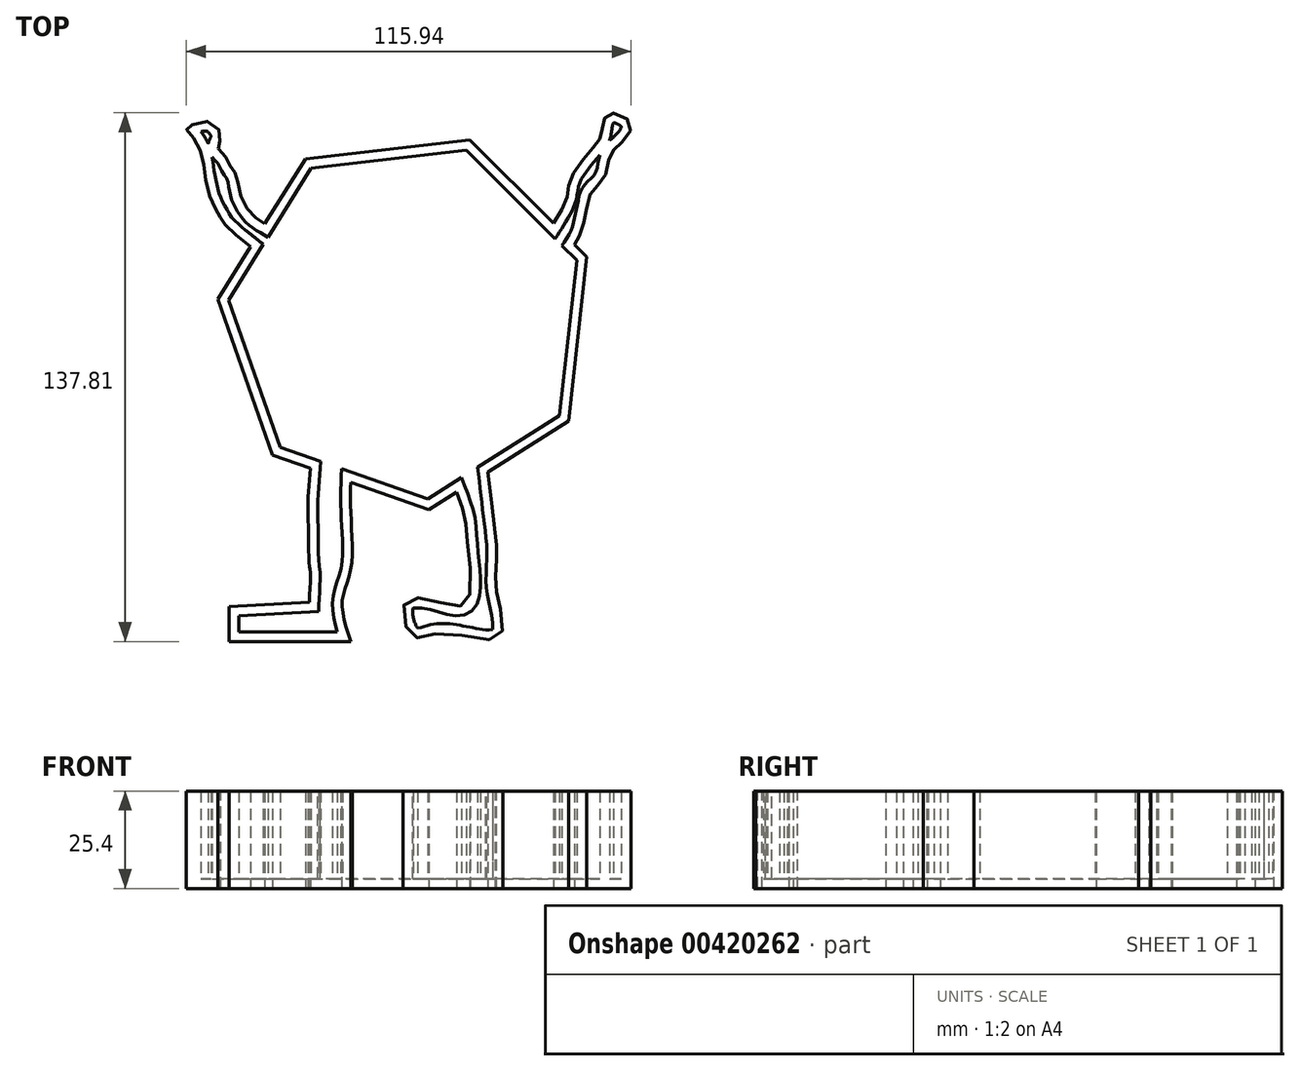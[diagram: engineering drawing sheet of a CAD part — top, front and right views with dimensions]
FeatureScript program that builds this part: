
annotation { "Feature Type Name" : "Feature", "Feature Type Description" : "" }
export const myFeature = defineFeature(function(context is Context, id is Id, definition is map)
    precondition{}
    {
        {
            var Q0;
            Q0=qCreatedBy(makeId("Top.planeOp"),FACE);
            var sketch = newSketch(context, id + "F0", { "sketchPlane" : qUnion([Q0])});
            skCircle(sketch, "E0.cCircle", {"center": v(-8.6, 19.06) * mm, "radius": 44.77 * mm, "construction": true});
            skLineSegment(sketch, "E0.0", {"start": v(33.53, -7.29) * mm, "end": v(-2.93, -30.3) * mm});
            skLineSegment(sketch, "E0.1", {"start": v(-2.93, -30.3) * mm, "end": v(-43.65, -16.15) * mm});
            skLineSegment(sketch, "E0.2", {"start": v(-43.65, -16.15) * mm, "end": v(-57.98, 24.52) * mm});
            skLineSegment(sketch, "E0.3", {"start": v(-57.98, 24.52) * mm, "end": v(-35.11, 61.08) * mm});
            skLineSegment(sketch, "E0.4", {"start": v(-35.11, 61.08) * mm, "end": v(7.72, 66) * mm});
            skLineSegment(sketch, "E0.5", {"start": v(7.72, 66) * mm, "end": v(38.27, 35.57) * mm});
            skLineSegment(sketch, "E0.6", {"start": v(38.27, 35.57) * mm, "end": v(33.53, -7.29) * mm});
            skPoint(sketch, "E0.0.midPoint", {"position": v(15.3, -18.8) * mm});
            skFitSpline(sketch, "E1", {"points": [v(-49.4, 38.23) * mm, v(-56.11, 44.03) * mm, v(-57.46, 46.18) * mm, v(-59.6, 50.2) * mm, v(-61.48, 58.26) * mm, v(-63.1, 64.7) * mm, v(-66.05, 68.73) * mm, v(-66.05, 69) * mm, v(-60.68, 70.88) * mm, v(-57.19, 66.85) * mm, v(-58, 64.17) * mm, v(-55.85, 61.48) * mm, v(-54.5, 58.8) * mm, v(-53.16, 56.92) * mm, v(-52.09, 51.82) * mm, v(-48.87, 46.45) * mm, v(-45.7, 44.14) * mm], "startDerivative": vector(-91.07, 72.12) * mm, "endDerivative": vector(53.16, -31.9) * mm});
            skFitSpline(sketch, "E2", {"points": [v(29.52, 44.29) * mm, v(33.02, 51.01) * mm, v(33.83, 55.3) * mm, v(38.66, 62.56) * mm, v(41.62, 66.31) * mm, v(42.42, 70.07) * mm, v(44.3, 73.03) * mm, v(49.67, 70.34) * mm, v(47.25, 65.24) * mm, v(44.3, 62.02) * mm, v(42.69, 56.11) * mm, v(39.2, 52.08) * mm, v(38.4, 48.86) * mm, v(38.13, 47.79) * mm, v(36.78, 42.15) * mm, v(35.03, 38.8) * mm], "startDerivative": vector(53.17, 85.15) * mm, "endDerivative": vector(-31.39, -47.16) * mm});
            skFitSpline(sketch, "E3", {"points": [v(-33.83, -19.56) * mm, v(-34.37, -26.85) * mm, v(-34.37, -34.1) * mm, v(-34.1, -44.57) * mm, v(-33.83, -46.72) * mm, v(-34.1, -54.5) * mm], "startDerivative": vector(-3.23, -35.86) * mm, "endDerivative": vector(-2.52, -43.22) * mm});
            skPoint(sketch, "E4.1.internal.snap0", {"position": v(-23.3, -23.23) * mm});
            skPoint(sketch, "E4.2.internal.snap0", {"position": v(-23.3, -23.23) * mm});
            skPoint(sketch, "E4.4.internal.snap0", {"position": v(-23.3, -23.23) * mm});
            skFitSpline(sketch, "E4", {"points": [v(-23.3, -23.23) * mm, v(-23.3, -31.15) * mm, v(-23.3, -45.91) * mm, v(-25.5, -54.24) * mm, v(-23.3, -64.7) * mm], "startDerivative": vector(-0.97, -32.17) * mm, "endDerivative": vector(14.5, -43.59) * mm});
            skLineSegment(sketch, "E5", {"start": v(-23.3, -64.7) * mm, "end": v(-55.04, -64.7) * mm});
            skLineSegment(sketch, "E6", {"start": v(-55.04, -64.7) * mm, "end": v(-55.04, -55.58) * mm});
            skLineSegment(sketch, "E7", {"start": v(-55.04, -55.58) * mm, "end": v(-34.1, -54.5) * mm});
            skPoint(sketch, "E8.end.orphan", {"position": v(15.3, -54.5) * mm});
            skFitSpline(sketch, "E9", {"points": [v(12.49, -20.58) * mm, v(14.5, -37.6) * mm, v(14.77, -41.89) * mm, v(14.5, -49.14) * mm, v(15.3, -54.5) * mm, v(15.3, -63.63) * mm, v(0, -62.56) * mm, v(-7.25, -63.37) * mm, v(-9.13, -54.5) * mm, v(0, -54.5) * mm, v(6.98, -54.5) * mm, v(7.25, -40) * mm, v(6.44, -32.22) * mm, v(4.3, -25.74) * mm], "startDerivative": vector(22.66, -189.45) * mm, "endDerivative": vector(-37.89, 98.07) * mm});
            skSolve(sketch);
        }
        {
            var Q0;
            {var subQ0=sQuery(id+"F0.wireOp",EDGE,"E9");Q0=makeQuery(id+"F0.imprint","IMPRINT",FACE,{"disambiguationData":[TD([[makeQuery(id+"F0.imprint","IMPRINT",EDGE,{"derivedFrom":subQ0}),-1.0]])]});}
            var Q1;
            {var subQ1=sQuery(id+"F0.wireOp",EDGE,"E3");Q1=makeQuery(id+"F0.imprint","IMPRINT",FACE,{"disambiguationData":[TD([[makeQuery(id+"F0.imprint","IMPRINT",EDGE,{"derivedFrom":subQ1}),1.0]])]});}
            var Q2;
            {var subQ0=sQuery(id+"F0.wireOp",EDGE,"E1");Q2=makeQuery(id+"F0.imprint","IMPRINT",FACE,{"disambiguationData":[TD([[makeQuery(id+"F0.imprint","IMPRINT",EDGE,{"derivedFrom":subQ0}),-1.0]])]});}
            var Q3;
            {var subQ0=sQuery(id+"F0.wireOp",EDGE,"E2");Q3=makeQuery(id+"F0.imprint","IMPRINT",FACE,{"disambiguationData":[TD([[makeQuery(id+"F0.imprint","IMPRINT",EDGE,{"derivedFrom":subQ0}),-1.0]])]});}
            var Q4;
            {var subQ5=sQuery(id+"F0.wireOp",EDGE,"E0.2");Q4=makeQuery(id+"F0.imprint","IMPRINT",FACE,{"disambiguationData":[TD([[makeQuery(id+"F0.imprint","IMPRINT",EDGE,{"derivedFrom":subQ5}),-1.0]])]});}
            extrude(context, id + "F1", {"entities" : qUnion([Q0, Q1, Q2, Q3, Q4]), "depth" : 25.4 * mm});
        }
        {
            var Q0;
            Q0=makeQuery(id+"F1.opExtrude","CAP_FACE",FACE,{"disambiguationData":[OSD([sQuery(id+"F0.wireOp",EDGE,"E0.0"),sQuery(id+"F0.wireOp",EDGE,"E0.1"),sQuery(id+"F0.wireOp",EDGE,"E0.2"),sQuery(id+"F0.wireOp",EDGE,"E0.3"),sQuery(id+"F0.wireOp",EDGE,"E0.4"),sQuery(id+"F0.wireOp",EDGE,"E0.5"),sQuery(id+"F0.wireOp",EDGE,"E0.6"),sQuery(id+"F0.wireOp",EDGE,"E1"),sQuery(id+"F0.wireOp",EDGE,"E2"),sQuery(id+"F0.wireOp",EDGE,"E3"),sQuery(id+"F0.wireOp",EDGE,"E4"),sQuery(id+"F0.wireOp",EDGE,"E5"),sQuery(id+"F0.wireOp",EDGE,"E6"),sQuery(id+"F0.wireOp",EDGE,"E7"),sQuery(id+"F0.wireOp",EDGE,"E9")])],"isStart":false});
            shell(context, id + "F2", {"entities" : qUnion([Q0]), "thickness" : 2.54 * mm});
        }
    });
